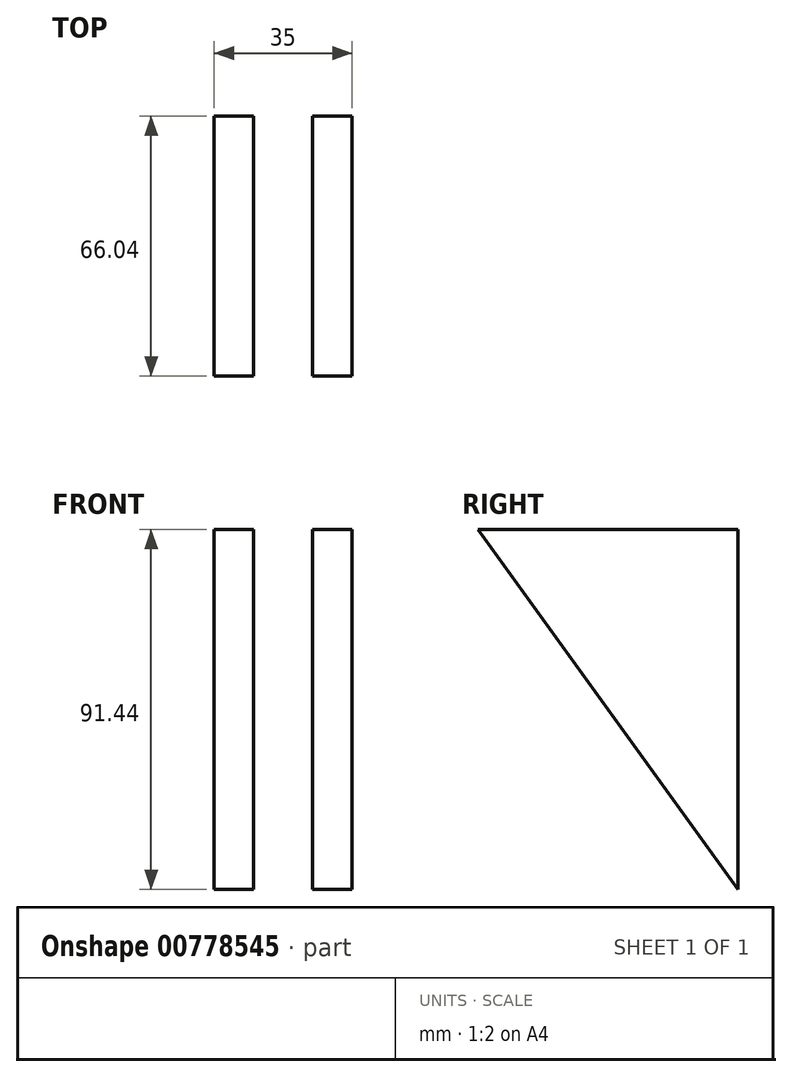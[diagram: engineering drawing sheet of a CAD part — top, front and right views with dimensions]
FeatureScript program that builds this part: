
annotation { "Feature Type Name" : "Feature", "Feature Type Description" : "" }
export const myFeature = defineFeature(function(context is Context, id is Id, definition is map)
    precondition{}
    {
        {
            var Q0;
            Q0=qCreatedBy(makeId("Top.planeOp"),FACE);
            var sketch = newSketch(context, id + "F0", { "sketchPlane" : qUnion([Q0])});
            skLineSegment(sketch, "E0.bottom", {"start": v(-21.69, 76.36) * mm, "end": v(-11.69, 76.36) * mm});
            skLineSegment(sketch, "E0.top", {"start": v(-21.69, 0.16) * mm, "end": v(-11.69, 0.16) * mm});
            skLineSegment(sketch, "E0.left", {"start": v(-21.69, 76.36) * mm, "end": v(-21.69, 0.16) * mm});
            skLineSegment(sketch, "E0.right", {"start": v(-11.69, 76.36) * mm, "end": v(-11.69, 0.16) * mm});
            skPoint(sketch, "E1.firstSnap0", {"position": v(-16.69, 76.36) * mm});
            skLineSegment(sketch, "E1.bottom", {"start": v(3.31, 76.36) * mm, "end": v(13.31, 76.36) * mm});
            skLineSegment(sketch, "E1.top", {"start": v(3.31, 0.16) * mm, "end": v(13.31, 0.16) * mm});
            skLineSegment(sketch, "E1.left", {"start": v(3.31, 76.36) * mm, "end": v(3.31, 0.16) * mm});
            skLineSegment(sketch, "E1.right", {"start": v(13.31, 76.36) * mm, "end": v(13.31, 0.16) * mm});
            skSolve(sketch);
        }
        {
            var Q0;
            Q0 = qSketchRegion(id + "F0", true);
            extrude(context, id + "F1", {"entities" : qUnion([Q0]), "depth" : 101.6 * mm, "offsetDistance" : 25.4 * mm});
        }
        {
            var Q0;
            Q0=makeQuery(id+"F1.opExtrude","SWEPT_FACE",FACE,{"disambiguationData":[OSD([sQuery(id+"F0.wireOp",EDGE,"E1.right")])]});
            var sketch = newSketch(context, id + "F2", { "sketchPlane" : qUnion([Q0])});
            skLineSegment(sketch, "E2", {"start": v(76.36, 0) * mm, "end": v(76.36, 10) * mm});
            skLineSegment(sketch, "E3", {"start": v(76.36, 10) * mm, "end": v(10.16, 10) * mm});
            skLineSegment(sketch, "E4", {"start": v(10.16, 10) * mm, "end": v(10.16, 101.6) * mm});
            skLineSegment(sketch, "E5", {"start": v(10.16, 101.6) * mm, "end": v(0.16, 101.6) * mm});
            skLineSegment(sketch, "E6", {"start": v(0.16, 101.6) * mm, "end": v(0.16, 0) * mm});
            skLineSegment(sketch, "E7", {"start": v(0.16, 0) * mm, "end": v(76.36, 0) * mm});
            skSolve(sketch);
        }
        {
            var Q0;
            Q0=makeQuery(id+"F2.imprint","IMPRINT",FACE,{"disambiguationData":[TD([[makeQuery(id+"F2.imprint","IMPRINT",EDGE,{"derivedFrom":sQuery(id+"F2.wireOp",EDGE,"E2")}),-1.0]])]});
            var Q1;
            Q1=makeQuery(id+"F1.opExtrude","SWEPT_FACE",FACE,{"disambiguationData":[OSD([sQuery(id+"F0.wireOp",EDGE,"E0.left")])]});
            extrude(context, id + "F3", {"entities" : qUnion([Q0]), "depth" : 50.8 * mm, "offsetDistance" : 25.4 * mm, "hasSecondDirection" : true, "secondDirectionBound" : SecondDirectionBoundingType.UP_TO_SURFACE, "secondDirectionOppositeDirection" : true, "secondDirectionDepth" : 25.4 * mm, "secondDirectionBoundEntityFace" : qUnion([Q1]), "hasSecondDirectionOffset" : true, "secondDirectionOffsetDistance" : 50.8 * mm, "secondDirectionOffsetOppositeDirection" : true});
        }
        {
            var Q0;
            Q0=makeQuery(id+"F3.opExtrude","SWEPT_FACE",FACE,{"disambiguationData":[OSD([sQuery(id+"F2.wireOp",EDGE,"E7")])]});
            var sketch = newSketch(context, id + "F4", { "sketchPlane" : qUnion([Q0])});
            skLineSegment(sketch, "E8", {"start": v(13.31, -76.36) * mm, "end": v(64.11, -10.16) * mm});
            skLineSegment(sketch, "E9", {"start": v(64.11, -10.16) * mm, "end": v(64.11, -76.36) * mm});
            skLineSegment(sketch, "E10", {"start": v(64.11, -76.36) * mm, "end": v(13.31, -76.36) * mm});
            skLineSegment(sketch, "E11", {"start": v(-72.49, -10.16) * mm, "end": v(-72.49, -76.36) * mm});
            skLineSegment(sketch, "E12", {"start": v(-72.49, -76.36) * mm, "end": v(-21.69, -76.36) * mm});
            skLineSegment(sketch, "E13", {"start": v(-21.69, -76.36) * mm, "end": v(-72.49, -10.16) * mm});
            skSolve(sketch);
        }
        {
            var Q0;
            Q0 = qSketchRegion(id + "F4", true);
            extrude(context, id + "F5", {"entities" : qUnion([Q0]), "operationType" : NewBodyOperationType.REMOVE, "oppositeDirection" : true, "depth" : 25.4 * mm, "offsetDistance" : 25.4 * mm});
        }
        {
            var Q0;
            Q0=makeQuery(id+"F3.opExtrude","SWEPT_FACE",FACE,{"disambiguationData":[OSD([sQuery(id+"F2.wireOp",EDGE,"E6")])]});
            var sketch = newSketch(context, id + "F6", { "sketchPlane" : qUnion([Q0])});
            skLineSegment(sketch, "E14", {"start": v(-21.69, 101.6) * mm, "end": v(-34.39, 10) * mm});
            skLineSegment(sketch, "E15", {"start": v(-34.39, 10) * mm, "end": v(-72.49, 10) * mm});
            skLineSegment(sketch, "E16", {"start": v(-72.49, 10) * mm, "end": v(-72.49, 101.6) * mm});
            skLineSegment(sketch, "E17", {"start": v(-72.49, 101.6) * mm, "end": v(-21.69, 101.6) * mm});
            skLineSegment(sketch, "E18", {"start": v(13.31, 101.6) * mm, "end": v(64.11, 101.6) * mm});
            skLineSegment(sketch, "E19", {"start": v(64.11, 101.6) * mm, "end": v(64.11, 10) * mm});
            skLineSegment(sketch, "E20", {"start": v(64.11, 10) * mm, "end": v(26.01, 10) * mm});
            skLineSegment(sketch, "E21", {"start": v(26.01, 10) * mm, "end": v(13.31, 101.6) * mm});
            skSolve(sketch);
        }
        {
            var Q0;
            Q0 = qSketchRegion(id + "F6", true);
            extrude(context, id + "F7", {"entities" : qUnion([Q0]), "operationType" : NewBodyOperationType.REMOVE, "oppositeDirection" : true, "depth" : 25.4 * mm, "offsetDistance" : 25.4 * mm});
        }
        {
            var Q0;
            Q0=qCreatedBy(makeId("Right.planeOp"),FACE);
            var sketch = newSketch(context, id + "F8", { "sketchPlane" : qUnion([Q0])});
            skLineSegment(sketch, "E22", {"start": v(10.32, 101.6) * mm, "end": v(76.36, 101.6) * mm});
            skLineSegment(sketch, "E23", {"start": v(76.36, 101.6) * mm, "end": v(76.36, 10.16) * mm});
            skLineSegment(sketch, "E24", {"start": v(76.36, 10.16) * mm, "end": v(10.32, 101.6) * mm});
            skSolve(sketch);
        }
        {
            var Q0;
            Q0 = qSketchRegion(id + "F8", true);
            extrude(context, id + "F9", {"entities" : qUnion([Q0]), "operationType" : NewBodyOperationType.INTERSECT, "oppositeDirection" : true, "depth" : 127 * mm, "offsetDistance" : 25.4 * mm, "hasSecondDirection" : true, "secondDirectionOppositeDirection" : false, "secondDirectionDepth" : 50.8 * mm});
        }
    });
